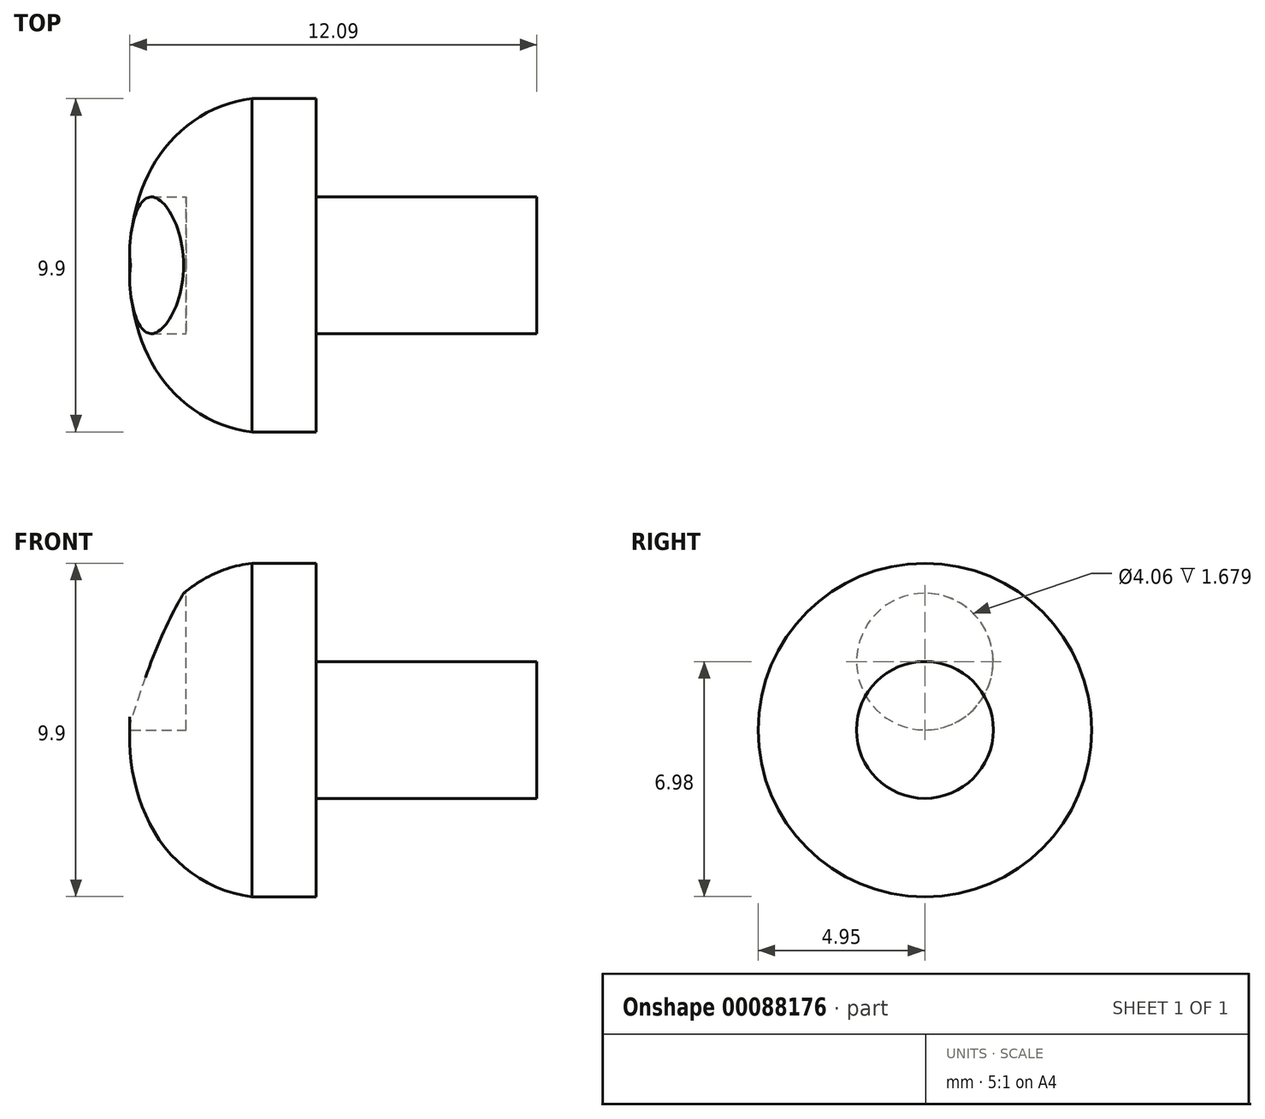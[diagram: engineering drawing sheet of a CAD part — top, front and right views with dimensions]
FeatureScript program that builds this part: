
annotation { "Feature Type Name" : "Feature", "Feature Type Description" : "" }
export const myFeature = defineFeature(function(context is Context, id is Id, definition is map)
    precondition{}
    {
        {
            var Q0;
            Q0=qCreatedBy(makeId("Front.planeOp"),FACE);
            var sketch = newSketch(context, id + "F0", { "sketchPlane" : qUnion([Q0])});
            skLineSegment(sketch, "E0", {"start": v(0, 0) * mm, "end": v(-12.07, 0) * mm});
            skLineSegment(sketch, "E1", {"start": v(0, 0) * mm, "end": v(0, 2.03) * mm});
            skLineSegment(sketch, "E2", {"start": v(0, 2.03) * mm, "end": v(-6.56, 2.03) * mm});
            skLineSegment(sketch, "E3", {"start": v(-6.56, 2.03) * mm, "end": v(-6.56, 4.95) * mm});
            skLineSegment(sketch, "E4", {"start": v(-6.56, 4.95) * mm, "end": v(-8.46, 4.95) * mm});
            skFitSpline(sketch, "E5", {"points": [v(-12.07, 0) * mm, v(-11.27, 3.19) * mm, v(-8.46, 4.95) * mm], "startDerivative": vector(-0.6, 4.91) * mm, "endDerivative": vector(6.37, 0.7) * mm});
            skLineSegment(sketch, "E6", {"start": v(0, 0) * mm, "end": v(0, 3.18) * mm, "construction": true});
            skSolve(sketch);
        }
        {
            var Q0;
            Q0 = qSketchRegion(id + "F0", true);
            var Q1;
            Q1=sQuery(id+"F0.wireOp",EDGE,"E0");
            revolve(context, id + "F1", {"entities" : qUnion([Q0]), "axis" : qUnion([Q1]), "revolveType" : RevolveType.FULL});
        }
        {
            var Q0;
            Q0=qCreatedBy(makeId("Right.planeOp"),FACE);
            var sketch = newSketch(context, id + "F2", { "sketchPlane" : qUnion([Q0])});
            skLineSegment(sketch, "E7", {"start": v(0, 0) * mm, "end": v(0, 2.03) * mm, "construction": true});
            skCircle(sketch, "E8", {"center": v(0, 2.03) * mm, "radius": 2.03 * mm});
            skSolve(sketch);
        }
        {
            var Q0;
            Q0 = qSketchRegion(id + "F2", true);
            extrude(context, id + "F3", {"entities" : qUnion([Q0]), "operationType" : NewBodyOperationType.REMOVE, "oppositeDirection" : true, "depth" : 25.4 * mm, "hasSecondDirection" : true, "secondDirectionOppositeDirection" : true, "secondDirectionDepth" : 10.4 * mm});
        }
    });
